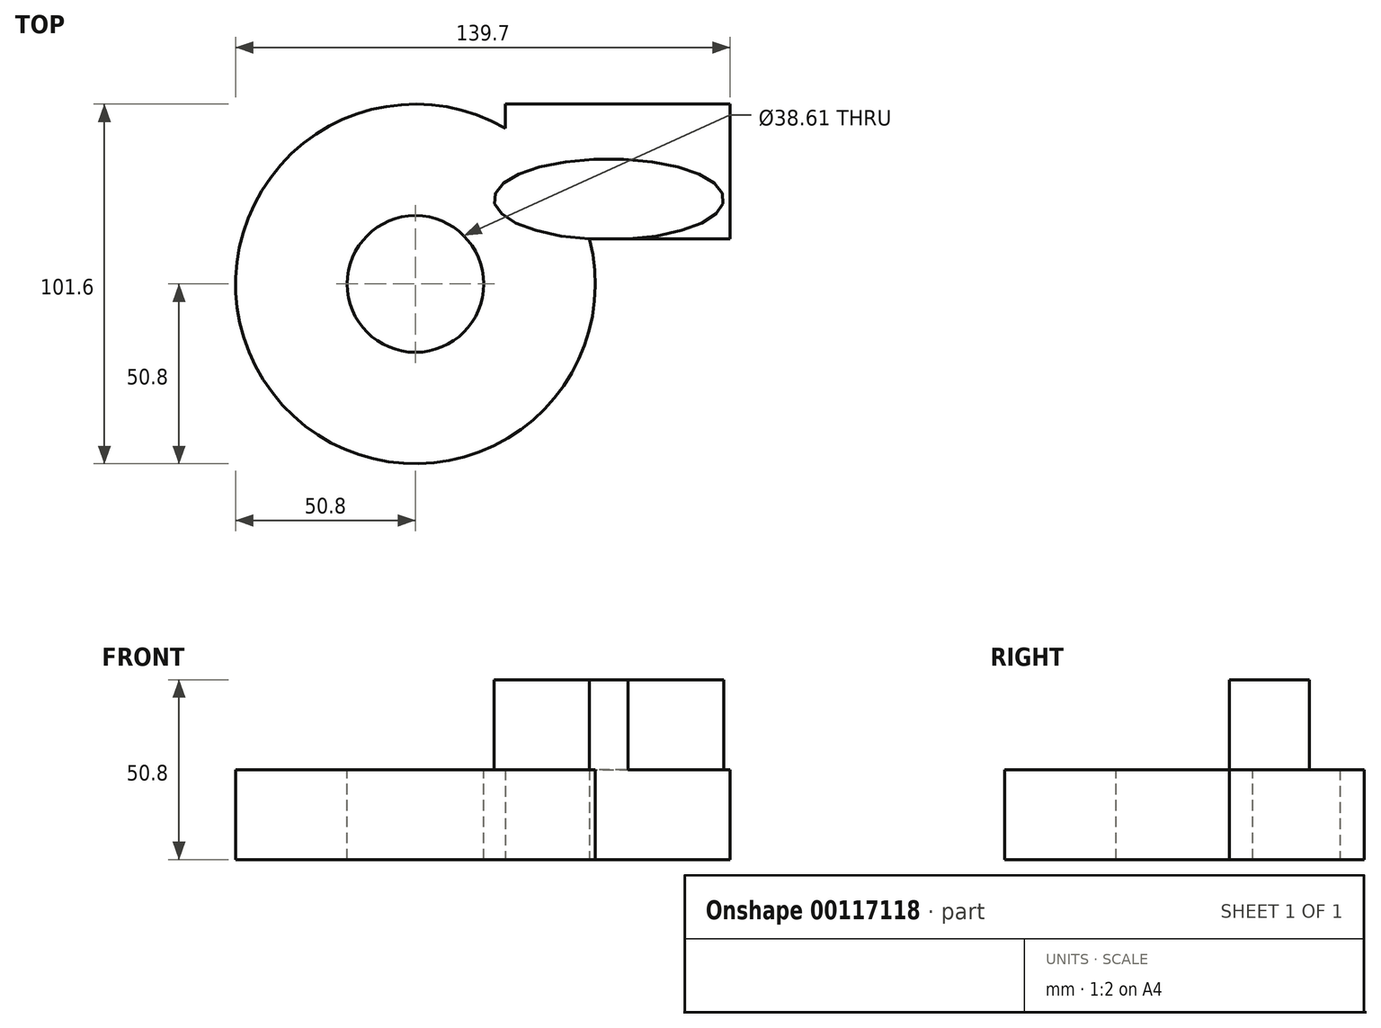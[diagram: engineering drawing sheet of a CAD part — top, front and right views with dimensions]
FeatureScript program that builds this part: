
annotation { "Feature Type Name" : "Feature", "Feature Type Description" : "" }
export const myFeature = defineFeature(function(context is Context, id is Id, definition is map)
    precondition{}
    {
        {
            var Q0;
            Q0=qCreatedBy(makeId("Top.planeOp"),FACE);
            var sketch = newSketch(context, id + "F0", { "sketchPlane" : qUnion([Q0])});
            skArc(sketch, "E0", {"start": v(25.4, 44) * mm, "mid": v(-40.44, -30.74) * mm, "end": v(49.19, 12.7) * mm});
            skLineSegment(sketch, "E1.bottom", {"start": v(49.19, 12.7) * mm, "end": v(88.9, 12.7) * mm});
            skLineSegment(sketch, "E1.top", {"start": v(25.4, 50.8) * mm, "end": v(88.9, 50.8) * mm});
            skLineSegment(sketch, "E1.left", {"start": v(25.4, 44) * mm, "end": v(25.4, 50.8) * mm});
            skLineSegment(sketch, "E1.right", {"start": v(88.9, 12.7) * mm, "end": v(88.9, 50.8) * mm});
            skSolve(sketch);
        }
        {
            var Q0;
            Q0 = qSketchRegion(id + "F0", true);
            extrude(context, id + "F1", {"entities" : qUnion([Q0]), "depth" : 25.4 * mm});
        }
        {
            var Q0;
            Q0=makeQuery(id+"F1.opExtrude","CAP_FACE",FACE,{"disambiguationData":[OSD([sQuery(id+"F0.wireOp",EDGE,"E0"),sQuery(id+"F0.wireOp",EDGE,"E1.bottom"),sQuery(id+"F0.wireOp",EDGE,"E1.top"),sQuery(id+"F0.wireOp",EDGE,"E1.left"),sQuery(id+"F0.wireOp",EDGE,"E1.right")])],"isStart":false});
            var sketch = newSketch(context, id + "F2", { "sketchPlane" : qUnion([Q0])});
            skCircle(sketch, "E2", {"center": v(0, 0) * mm, "radius": 19.3 * mm});
            skSolve(sketch);
        }
        {
            var Q0;
            Q0 = qSketchRegion(id + "F2", true);
            extrude(context, id + "F3", {"entities" : qUnion([Q0]), "operationType" : NewBodyOperationType.REMOVE, "oppositeDirection" : true, "depth" : 25.4 * mm});
        }
        {
            var Q0;
            Q0=makeQuery(id+"F1.opExtrude","CAP_FACE",FACE,{"disambiguationData":[OSD([sQuery(id+"F0.wireOp",EDGE,"E0"),sQuery(id+"F0.wireOp",EDGE,"E1.bottom"),sQuery(id+"F0.wireOp",EDGE,"E1.top"),sQuery(id+"F0.wireOp",EDGE,"E1.left"),sQuery(id+"F0.wireOp",EDGE,"E1.right")])],"isStart":false});
            var sketch = newSketch(context, id + "F4", { "sketchPlane" : qUnion([Q0])});
            skEllipse(sketch, "E3", {"center": v(54.64, 23.94) * mm, "majorRadius": 32.43 * mm, "minorRadius": 11.4 * mm, "majorAxis": v(1, 0)});
            skSolve(sketch);
        }
        {
            var Q0;
            {var subQ0=sQuery(id+"F4.wireOp",EDGE,"E3");var subQ1=makeQuery(id+"F1.opExtrude","CAP_EDGE",EDGE,{"disambiguationData":[OSD([sQuery(id+"F0.wireOp",EDGE,"E1.bottom")])],"isStart":false});var subQ3=makeQuery(id+"F4.imprint","INTERSECT",VERTEX,{"derivedFrom":[subQ1,subQ0]});Q0=makeQuery(id+"F4.imprint","IMPRINT",FACE,{"disambiguationData":[TD([[makeQuery(id+"F4.imprint","IMPRINT",EDGE,{"disambiguationData":[TD([[subQ3,-1.0]])],"derivedFrom":subQ0}),1.0]])]});}
            extrude(context, id + "F5", {"entities" : qUnion([Q0]), "operationType" : NewBodyOperationType.ADD, "depth" : 25.4 * mm});
        }
    });
